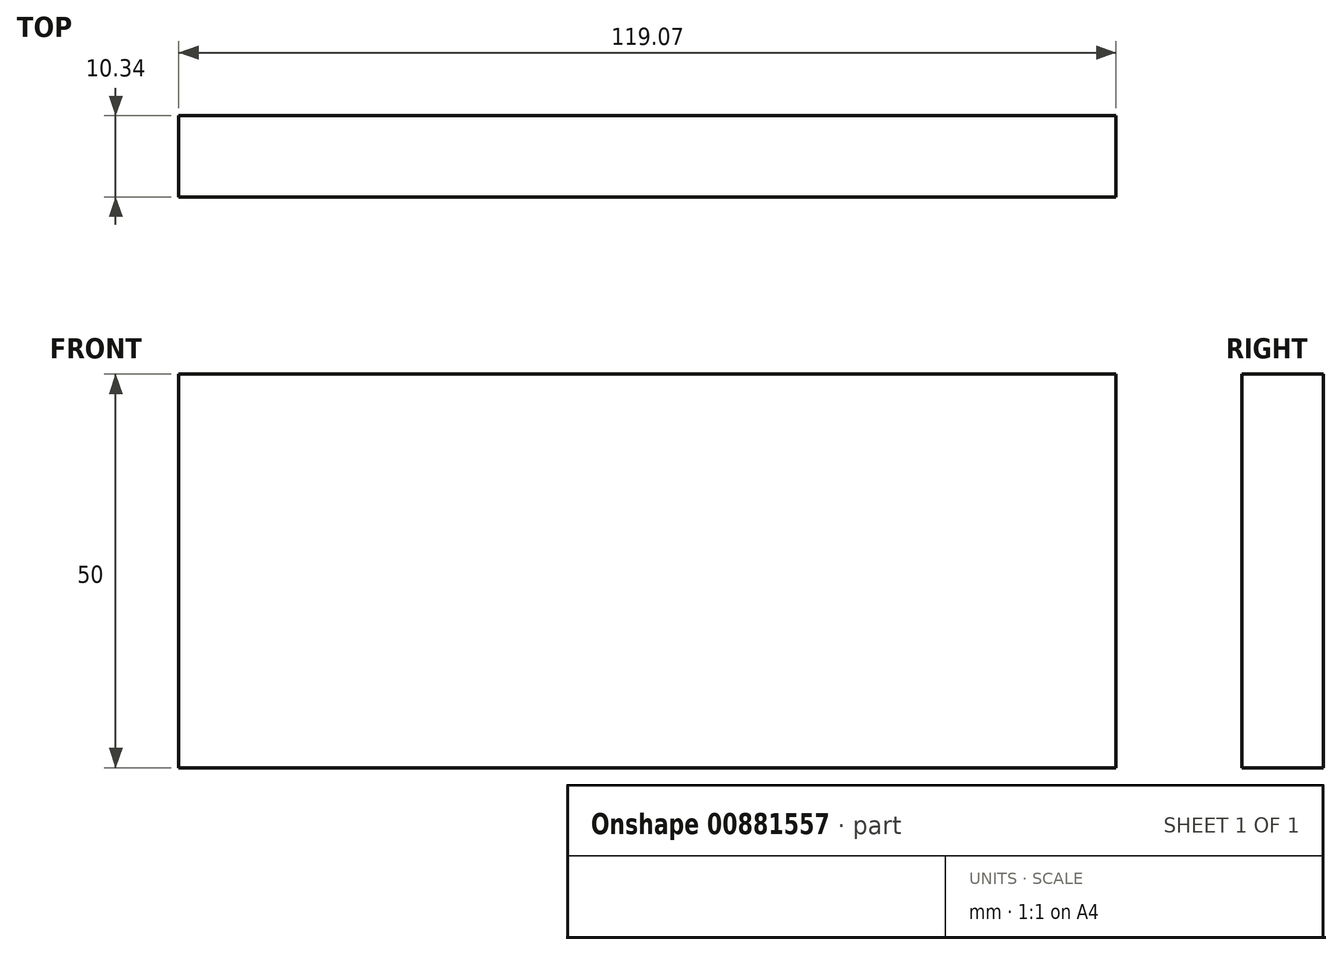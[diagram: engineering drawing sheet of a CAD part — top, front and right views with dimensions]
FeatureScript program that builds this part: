
annotation { "Feature Type Name" : "Feature", "Feature Type Description" : "" }
export const myFeature = defineFeature(function(context is Context, id is Id, definition is map)
    precondition{}
    {
        {
            var Q0;
            Q0=qCreatedBy(makeId("Top.planeOp"),FACE);
            var sketch = newSketch(context, id + "F0", { "sketchPlane" : qUnion([Q0])});
            skLineSegment(sketch, "E0.bottom", {"start": v(-87.33, -23.02) * mm, "end": v(31.74, -23.02) * mm});
            skLineSegment(sketch, "E0.top", {"start": v(-87.33, -12.68) * mm, "end": v(31.74, -12.68) * mm});
            skLineSegment(sketch, "E0.left", {"start": v(-87.33, -23.02) * mm, "end": v(-87.33, -12.68) * mm});
            skLineSegment(sketch, "E0.right", {"start": v(31.74, -23.02) * mm, "end": v(31.74, -12.68) * mm});
            skSolve(sketch);
        }
        {
            var Q0;
            Q0=makeQuery(id+"F0.imprint","IMPRINT",FACE,{"disambiguationData":[TD([[makeQuery(id+"F0.imprint","IMPRINT",EDGE,{"derivedFrom":sQuery(id+"F0.wireOp",EDGE,"E0.bottom")}),1.0]])]});
            extrude(context, id + "F1", {"entities" : qUnion([Q0]), "depth" : 50 * mm, "offsetDistance" : 25.4 * mm});
        }
    });
